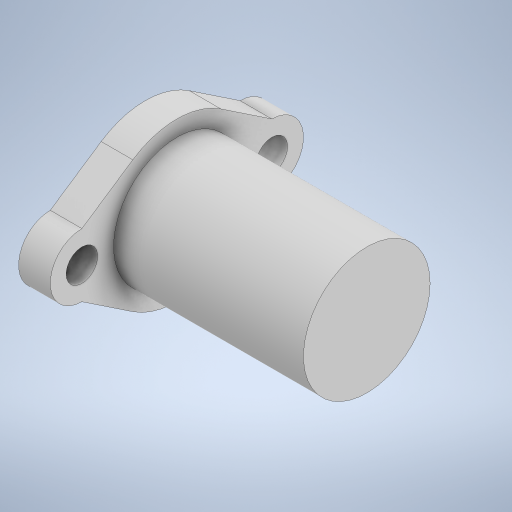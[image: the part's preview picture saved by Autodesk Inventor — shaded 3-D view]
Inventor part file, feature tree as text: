
AUTODESK INVENTOR PART (.ipt)
format: ipt  version: 2023 (Build 270158000, 158)  size: 255,488 bytes
history: native  units: mm
features: extrude x2, sketch x2, other x1
ambient origin geometry x8: Origin, YZ Plane, XZ Plane, XY Plane, X Axis, Y Axis, Z Axis, Center Point
bodies: Body1 (feature_tree)
feature tree (5):
  other  "Твердое тело1"
  extrude  "Выдавливание1"  Depth=50.0mm
  extrude  "Выдавливание2"  Depth=5.0mm
  sketch  "Эскиз1"
  sketch  "Эскиз2"
